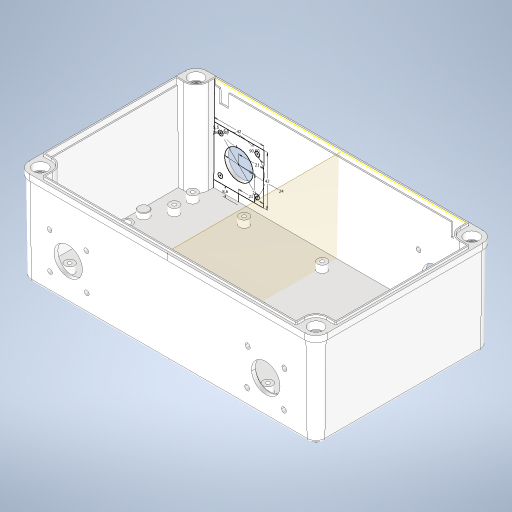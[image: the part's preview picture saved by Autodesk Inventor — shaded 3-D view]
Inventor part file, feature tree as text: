
AUTODESK INVENTOR PART (.ipt)
format: ipt  version: 2024 (Build 280153000, 153)  size: 2,298,368 bytes
history: native  units: in
note: dims shown in document units (in); Inventor stores cm internally (conversion verified against a paired STEP export)
features: other x3, extrude x3, sketch x2, plane x1, mirror x1, projected_geometry x1
ambient origin geometry x8: Origin, YZ Plane, XZ Plane, XY Plane, X Axis, Y Axis, Z Axis, Center Point
bodies: Solid1 (feature_tree)
feature tree (11):
  other  "ORCF FILLETS"
  other  "LOCATING FASTENING BODY CIRCLE PATTERN AXIS"
  other  "Plane1"
  sketch  "Sketch2"  dims[d1=0.3386in d2=0.8268in]
  extrude  "Extrusion1"  Depth=0.8268in
  plane  "Work Plane3"
  extrude  "Extrusion2"  Depth=0.3937in
  mirror  "Mirror1"
  extrude  "Extrusion3"  TaperAngle=90.0deg  [1 undecoded]
  sketch  "Sketch4"  dims[d3=1.6535in d4=1.6535in d5=90.0deg d6=0.9449in d7=0.8268in d8=0.8268in d9=0.1575in d10=0.2165in d11=0.2165in d12=1.5748in d14=360.0deg d16=0.3937in d17=0.0in d19=-4.9568in d20=0.3937in d21=0.0in d22=0.0in d23=0.0in]
  projected_geometry  "Projected Loop1"
note: 1 required parameter value undecoded (feature->parameter linkage not recoverable at this tier; creation-order binding heuristic only, values carry confidence <= 0.55)
